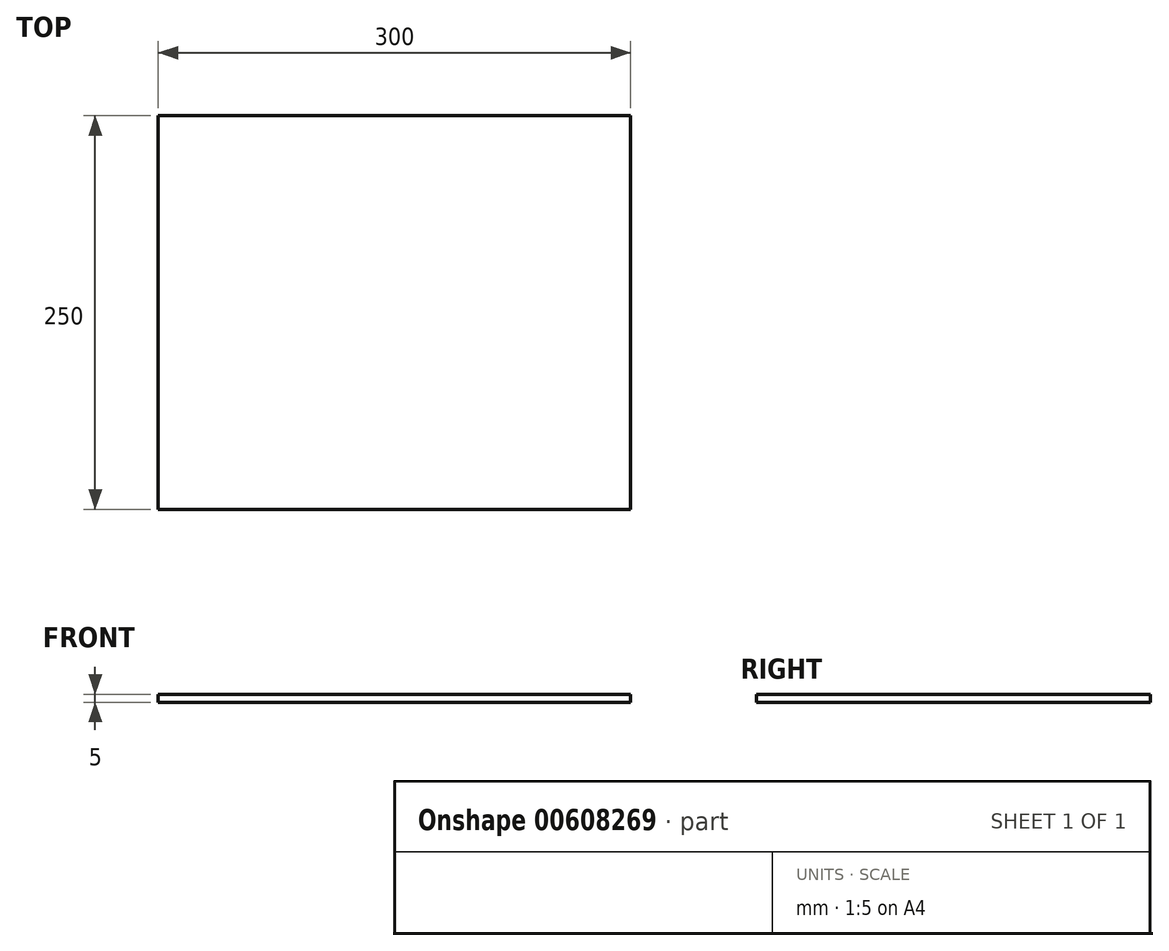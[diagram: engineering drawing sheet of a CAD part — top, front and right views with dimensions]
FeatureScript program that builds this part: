
annotation { "Feature Type Name" : "Feature", "Feature Type Description" : "" }
export const myFeature = defineFeature(function(context is Context, id is Id, definition is map)
    precondition{}
    {
        {
            var Q0;
            Q0=qCreatedBy(makeId("Top.planeOp"),FACE);
            var sketch = newSketch(context, id + "F0", { "sketchPlane" : qUnion([Q0])});
            skLineSegment(sketch, "E0.bottom", {"start": v(-150, 125) * mm, "end": v(150, 125) * mm});
            skLineSegment(sketch, "E0.top", {"start": v(-150, -125) * mm, "end": v(150, -125) * mm});
            skLineSegment(sketch, "E0.left", {"start": v(-150, 125) * mm, "end": v(-150, -125) * mm});
            skLineSegment(sketch, "E0.right", {"start": v(150, 125) * mm, "end": v(150, -125) * mm});
            skPoint(sketch, "E0.middle", {"position": v(0, 0) * mm});
            skSolve(sketch);
        }
        {
            var Q0;
            Q0 = qSketchRegion(id + "F0", true);
            extrude(context, id + "F1", {"entities" : qUnion([Q0]), "depth" : 5 * mm, "offsetDistance" : 25.4 * mm});
        }
    });
